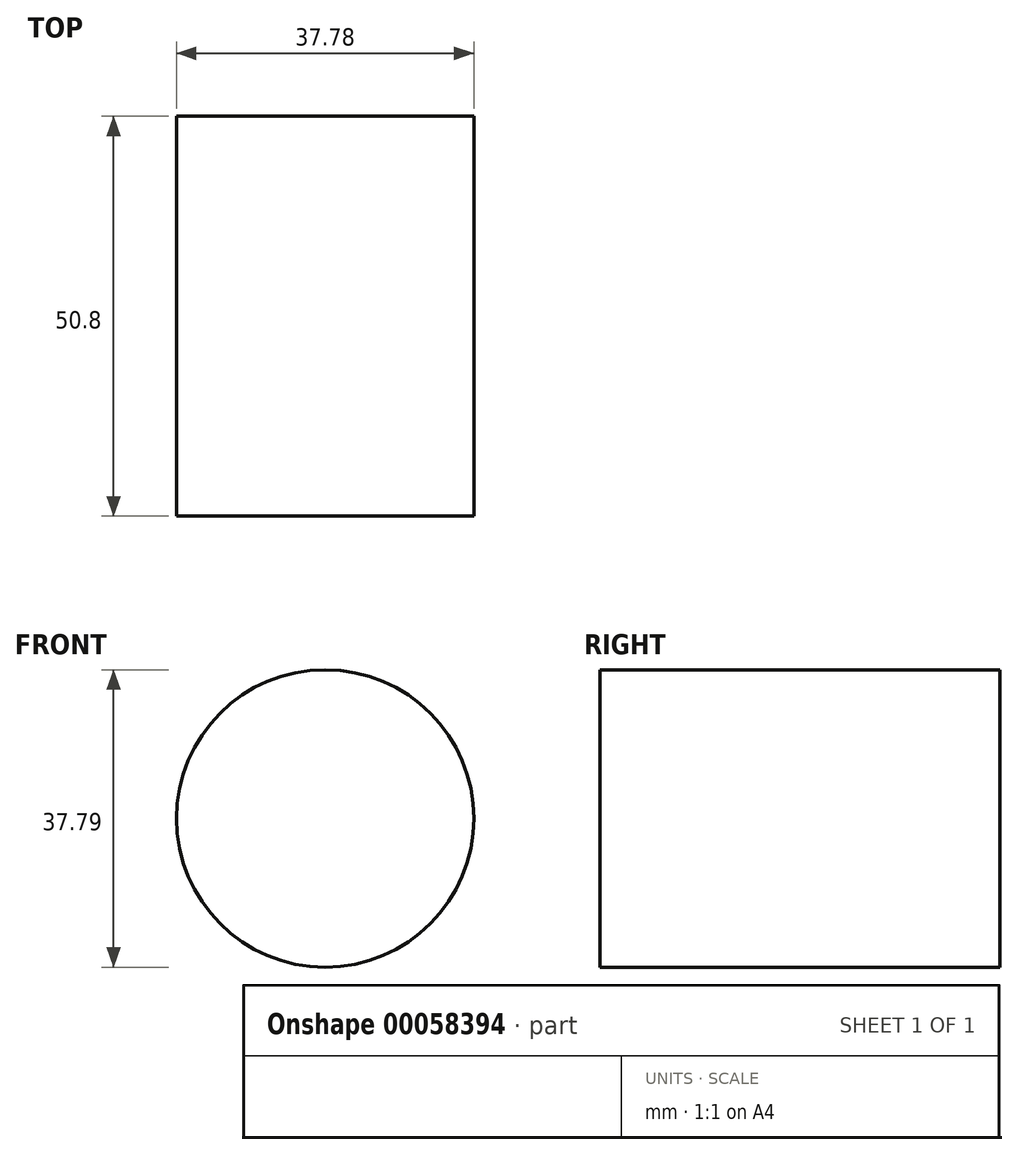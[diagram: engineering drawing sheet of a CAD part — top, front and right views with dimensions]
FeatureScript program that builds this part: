
annotation { "Feature Type Name" : "Feature", "Feature Type Description" : "" }
export const myFeature = defineFeature(function(context is Context, id is Id, definition is map)
    precondition{}
    {
        {
            var Q0;
            Q0=qCreatedBy(makeId("Front.planeOp"),FACE);
            var sketch = newSketch(context, id + "F0", { "sketchPlane" : qUnion([Q0])});
            skCircle(sketch, "E0", {"center": v(0, 3.76) * mm, "radius": 18.9 * mm});
            skSolve(sketch);
        }
        {
            var Q0;
            Q0 = qSketchRegion(id + "F0", true);
            extrude(context, id + "F1", {"entities" : qUnion([Q0]), "depth" : 50.8 * mm});
        }
    });
